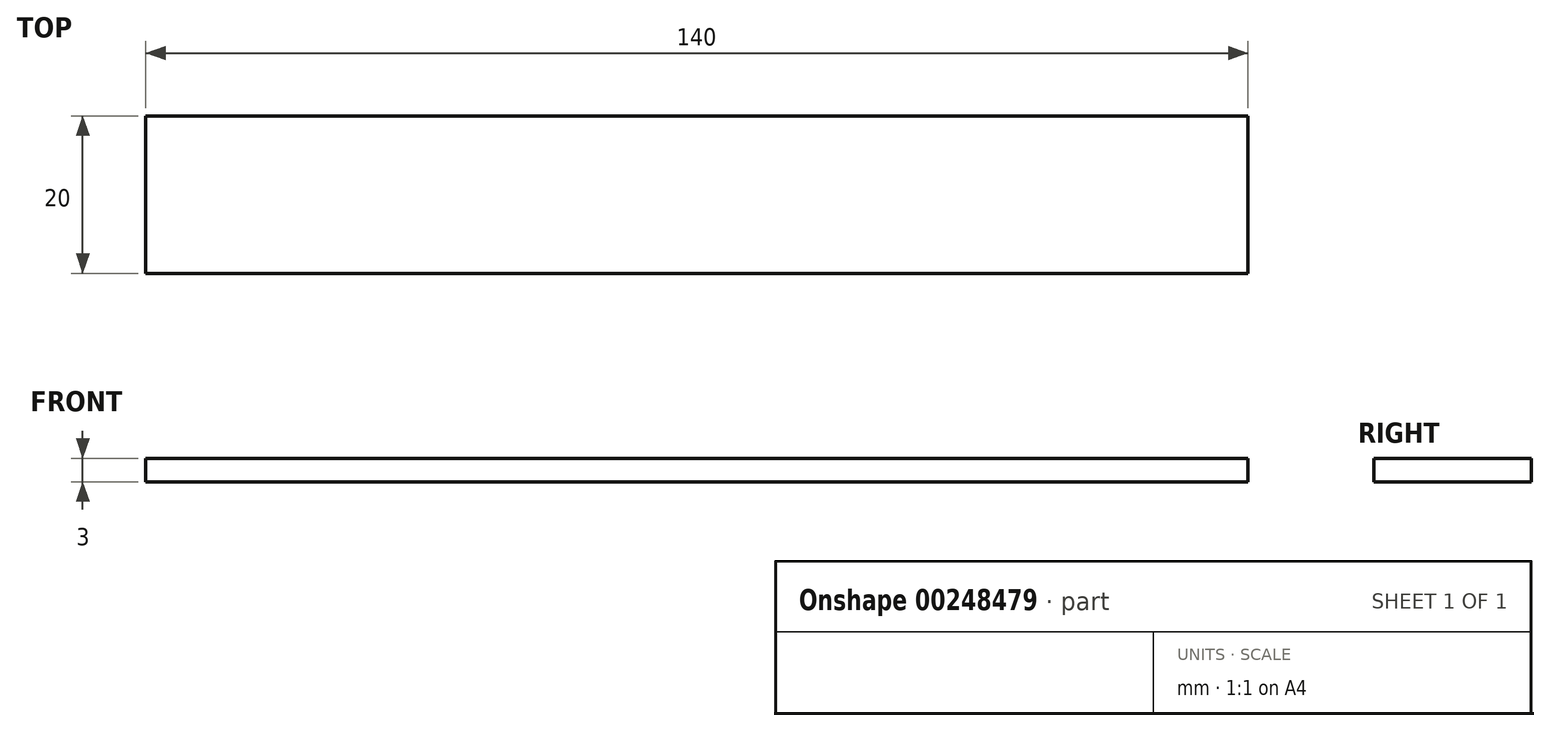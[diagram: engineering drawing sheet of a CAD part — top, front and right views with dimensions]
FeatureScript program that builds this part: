
annotation { "Feature Type Name" : "Feature", "Feature Type Description" : "" }
export const myFeature = defineFeature(function(context is Context, id is Id, definition is map)
    precondition{}
    {
        {
            var Q0;
            Q0=qCreatedBy(makeId("Top.planeOp"),FACE);
            var sketch = newSketch(context, id + "F0", { "sketchPlane" : qUnion([Q0])});
            skLineSegment(sketch, "E0.bottom", {"start": v(-71.57, 8.86) * mm, "end": v(68.43, 8.86) * mm});
            skLineSegment(sketch, "E0.top", {"start": v(-71.57, -11.14) * mm, "end": v(68.43, -11.14) * mm});
            skLineSegment(sketch, "E0.left", {"start": v(-71.57, 8.86) * mm, "end": v(-71.57, -11.14) * mm});
            skLineSegment(sketch, "E0.right", {"start": v(68.43, 8.86) * mm, "end": v(68.43, -11.14) * mm});
            skSolve(sketch);
        }
        {
            var Q0;
            Q0 = qSketchRegion(id + "F0", true);
            extrude(context, id + "F1", {"entities" : qUnion([Q0]), "depth" : 3 * mm});
        }
    });
